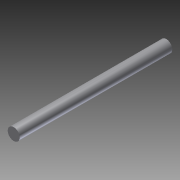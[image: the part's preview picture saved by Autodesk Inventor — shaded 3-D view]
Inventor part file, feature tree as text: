
AUTODESK INVENTOR PART (.ipt)
format: ipt  version: 2012 (Build 160160000, 160)  size: 66,048 bytes
history: native  units: in
note: dims shown in document units (in); Inventor stores cm internally (conversion verified against a paired STEP export)
features: extrude x1, sketch x1
ambient origin geometry x8: Origin, YZ Plane, XZ Plane, XY Plane, X Axis, Y Axis, Z Axis, Center Point
bodies: Solid1 (feature_tree)
feature tree (2):
  extrude  "Extrusion1"  Depth=4.75in TaperAngle=0.0deg
  sketch  "Sketch1"  dims[d0=0.375in d1=4.75in d2=0.0in]
